# Revit family: 2019_ES_Ventana_QSystems_Q150_2-Hojas-Correderas
name_source: partatom
category: Windows
units: mm (PartAtom-declared; Revit-internal decimal feet)

## family parameters
Always vertical = Yes
Cut with Voids When Loaded = No
Host = Wall
OmniClass Number = 23.30.20.00
OmniClass Title = Windows
Room Calculation Point = No
Shared = No

## types (1)
- 1230x1480 mm
    Acabado = Anodizado, lacado y acabados
    AcidificacionAtmosferica = 0
    AcidificacionAtmosfericaPorUnidad = 0
    Acristalamiento = Cristal - Vidrio claro templado
    AguaConsumida = 0
    AguaConsumidaPorUnidad = 0
    Altura Máxima = 2800.000 mm
    Altura Mínima = 950.000 mm
    Altura Real = 1480.000 mm
    Altura de antepecho por defecto = 500.000 mm
    Altura maxima = 0.000 mm
    Altura minima = 0.000 mm
    Analytic Construction = 1/4 in Pilkington single glazing
    Ancho marco inferior = 140.300 mm
    Ancho marco lateral = 140.000 mm
    Ancho marco superior = 140.300 mm
    AnchoMarcoCentral = 103.000 mm
    AnchoPoliamidaHoja = 18.000 mm
    AnchoPoliamidaMarco = 34.000 mm
    Anchura Maxima = 3350.000 mm
    Anchura Minima = 600.000 mm
    Anchura Real = 1230.000 mm
    Area = 1.820 m²
    Autor = Bimetica Parametric Design Services, S.L.
    BIMsupport = https://bimsupport.info
    COBieCategoria = IfcWindow
    CambioClimatico = 0
    CambioClimaticoPorUnidad = 0
    Carpinteria Media 𝑈𝑓 = 3.798704
    Catálogo (URL) = https://qsystemsaluminio.com
    CerramientoExterior = Yes
    Clasificacion acustica = 29 (-1,-2) dB
    ConfiguracionPoliamidas = 268400 - 964000
    ControlHumos = No
    CosteEnergeticoKwh = 0
    CosteEnergeticoMj = 0 J
    CosteMantenimiento = 0
    Description = Ventana Corredera Elevable de 2 hojas de Aluminio modelo Q150 de QSystems
    DestruccionCapaOzonoEstratosferica = 0
    DestruccionCapaOzonoEstratosfericaPorUnidad = 0
    EmisionCO2 = 0
    Energia consumida = 0
    EnergiaNoRenovableConsumida = 0
    EnergiaNoRenovableConsumidaPorUnidad = 0
    EnergiaPrimariaTotalConsumida = 0
    EnergiaPrimariaTotalConsumidaPorUnidad = 0
    EnergiaRenovableConsumida = 0
    EnergiaRenovableConsumidaPorUnidad = 0
    EspesorPerfilesAluminio = 1.800 mm
    EstanqueidadAgua = Clase 7A
    Eutrofizacion = 0
    EutrofizacionPorUnidad = 0
    FactorSolarModificado = 0
    FactorSombra = 0
    FaltaDeRecursos = 0
    FaltaDeRecursosPorUnidad = 0
    FechaEmisionElementoBIM = 03/12/2021
    FechaVencimientoElementoBIM = 03/12/2022
    FormacionFotoquimicaOzono = 0
    FormacionFotoquimicaOzonoPorUnidad = 0
    Fraccion de area de acristalamiento = 0.55806
    Grosor Acristalamiento Real = 32.000 mm
    GrosorAcristalamiento = 32.000 mm
    GrosorHoja = 55.000 mm
    GrosorMarco = 150.000 mm
    GrosorMaximoAcristalamiento = 40.000 mm
    GrosorMinimoAcristalamiento = 6.000 mm
    Gubimclass Codigo = 30.10.20.10
    Gubimclass Titulo = Ventanas de fachadas
    Heat Transfer Coefficient (U) = 6.7018 W/(m²·K)
    Height = 1480.000 mm
    Historial = (RVT2019) Actualziación a estándar GDO-BIM y datos. (RVT2015) Creación del Elemento.
    IfcExportAs = IfcWindow
    IfcExportType = Corredera
    Infiltracion = 0
    InformacionTecnica = https://qsystemsaluminio.com
    Intercalario = Technoform Warm Edge
    Lw E = 0.4235
    Lw I = 0.4235
    Manija = Yes
    Manufacturer = QSystems
    Marcado CE = No
    Marco = Aluminio Anodizado, lacado
    MasterformatCodigo = 08 50 00
    MasterformatTitulo = Windows
    Model = Q150 2 hojas correderas
    Motorizada = No
    Numero de Licencia = XXX-XXXX9536
    OmniclassCodigo = 23-17 13 00
    OmniclassTitulo = Window
    Operation = Ventana corredera elevable de dos hojas con dos raíles
    Perimetro = 5420
    PermeabilidadAlAire = Clase 3
    Peso = 0.00 kg
    PesoMáximoDeLaHoja = 400.00 kg
    Plataforma descaga contenido BIM = www.bimetica.com
    Poliamida = Technoform polyamide
    Profundidad = 0.000 mm
    PuntoDeContacto = QSystems
    Referencia = Q150
    ReferenciaContacto = QSystems
    RepisaExterior = Yes
    RepisaInterior = Yes
    ResiduoInerte = 0
    ResiduoInertePorUnidad = 0
    ResiduoRadioactivo = 0
    ResiduoRadioactivoPorUnidad = 0
    ResiduosNoPeligrosos = 0
    ResiduosNoPeligrososPorUnidad = 0
    ResiduosPeligrosos = 0
    ResiduosPeligrososPorUnidad = 0
    ResistenciaAlViento = Clase C3
    SalidaEmergencia = No
    Serie = Q150
    Solar Heat Gain Coefficient = 0.86
    TelefonoContacto = +34 91 895 58 00
    Thermal Resistance (R) = 0.1492 (m²·K)/W
    Titular = Alueuropa S.A.
    Total Y𝑔 = 0.11
    Total 𝐴𝑓 = 0.805 m²
    Total 𝐴𝑔 = 1.015892
    Total 𝑈𝑔 = 1.3
    Total 𝑙𝑔 = 6.4916
    Transmitancia termica = 2.7965 W/(m²·K)
    UNSPSCCodigo = 30171612
    UNSPSCTitulo = Projected Windows
    URL = http://qsystemsaluminio.com
    URL Perfil BIM = https://bimetica.com
    URL Poliamida = http://www.technoform.es
    URL Poliamida - Catálogo = http://www.technoform.com
    URLProducto = https://qsystemsaluminio.com
    Uniclass2.0Codigo = Ss_15_50_25
    Uniclass2.0Titulo = Doors, Windows And Glazing Survey Systems
    Version = RVT2019
    Version Estandar GDO-BIM = GDO-BIM V02
    Visual Light Transmittance = 0.9
    Wall Closure = By host
    Width = 1230.000 mm
    Y𝑔 NC = 0.11
    Y𝑔 PIE = 0.11
    Y𝑔 PII = 0.11
    Y𝑔 PLE = 0.11
    Y𝑔 PLI = 0.11
    Y𝑔 PSE = 0.11
    Y𝑔 PSI = 0.11
    𝐴𝑓 NC = 0.138 m²
    𝐴𝑓 PIE = 0.073 m²
    𝐴𝑓 PII = 0.073 m²
    𝐴𝑓 PLE = 0.188 m²
    𝐴𝑓 PLI = 0.188 m²
    𝐴𝑓 PSE = 0.073 m²
    𝐴𝑓 PSI = 0.073 m²
    𝐴𝑔 VE = 0.507946
    𝐴𝑔 VI = 0.507946
    𝑈𝑓 NC = 5
    𝑈𝑓 PIE = 3.4
    𝑈𝑓 PII = 3.7
    𝑈𝑓 PLE = 3.4
    𝑈𝑓 PLI = 3.7
    𝑈𝑓 PSE = 3.4
    𝑈𝑓 PSI = 3.7
    𝑈𝑔 VE = 1.3
    𝑈𝑔 VI = 1.3
    𝑈𝑤 = 2.796541
    𝑙𝑔 NC = 2.3988
    𝑙𝑔 PIE = 0.4235
    𝑙𝑔 PII = 0.4235
    𝑙𝑔 PLE = 1.1994
    𝑙𝑔 PLI = 1.1994
    𝑙𝑔 PSE = 0.4235
    𝑙𝑔 PSI = 0.4235

## geometry (parser evidence)
native form markers: Blend x2
no freeform markers — native parametric forms only
